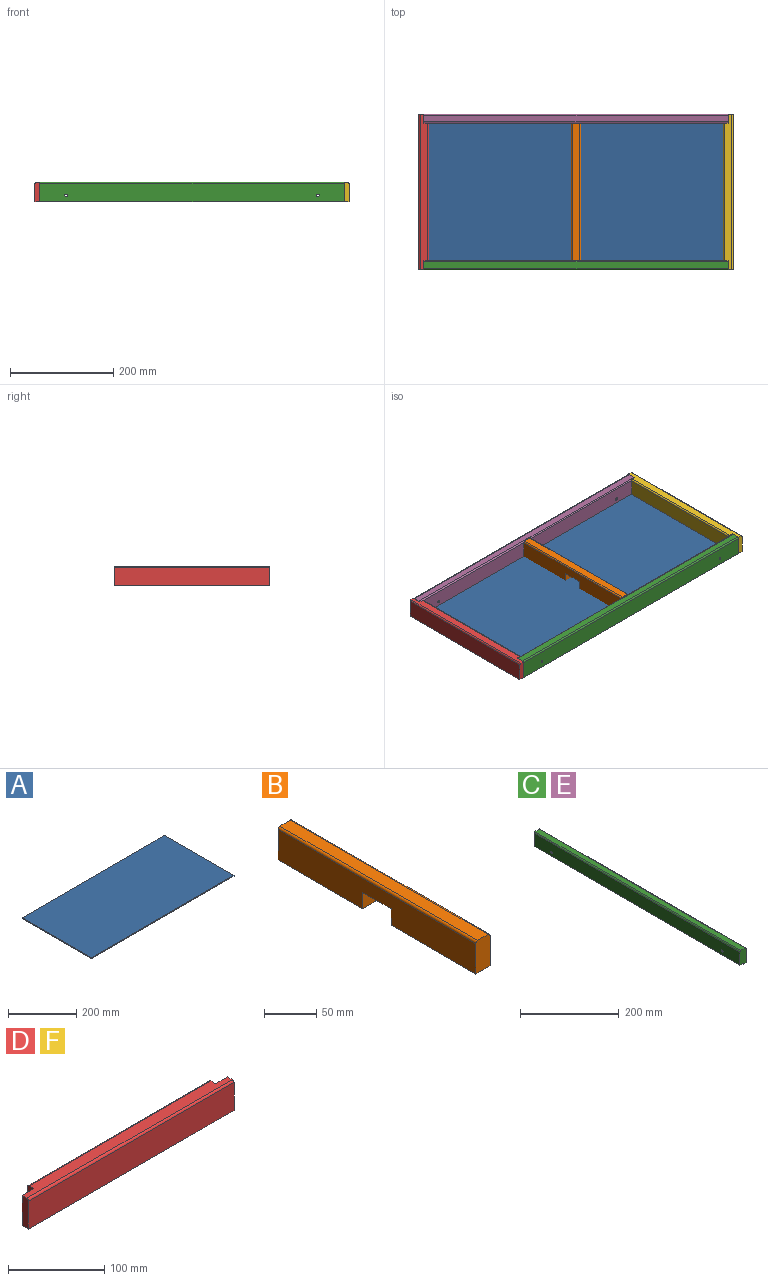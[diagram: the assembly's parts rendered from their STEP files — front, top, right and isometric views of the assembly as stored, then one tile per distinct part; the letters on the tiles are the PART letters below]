
ASSEMBLY  parts=6 mates=5
PART A: 6 faces, bbox 590.6x285.8x3.2 mm
  f0: plane 590.55x3.18mm, normal (0,-1,0), area 1875mm2, adj f1,f3,f4,f5
  f1: plane 285.75x3.18mm, normal (1,0,0), area 907.3mm2, adj f0,f2,f4,f5
  f2: plane 590.55x3.18mm, normal (0,1,0), area 1875mm2, adj f1,f3,f4,f5
  f3: plane 285.75x3.18mm, normal (-1,0,0), area 907.3mm2, adj f0,f2,f4,f5
  f4: plane 590.55x285.75mm, normal (0,0,1), area 168749.7mm2, adj f0,f1,f2,f3
  f5: plane 590.55x285.75mm, normal (0,0,-1), area 168749.7mm2, adj f0,f1,f2,f3
PART B: 12 faces, bbox 19.1x266.7x38.1 mm
  f0: plane 114.3x19.05mm, normal (0,0,-1), area 2177.4mm2, adj f1,f2,f3,f9
  f1: plane 266.7x35.56mm, normal (1,0,0), area 8758mm2, adj f0,f3,f4,f6,f7,f9,f10,f11
  f2: plane 266.7x35.56mm, normal (-1,0,0), area 8758mm2, adj f0,f3,f4,f6,f8,f9,f10,f11
  f3: plane 38.1x19.05mm, normal (0,-1,0), area 723mm2, adj f0,f1,f2,f5,f7,f8
  f4: plane 38.1x19.05mm, normal (0,1,0), area 723mm2, adj f1,f2,f5,f6,f7,f8
  f5: plane 266.7x13.97mm, normal (0,0,1), area 3725.8mm2, adj f3,f4,f7,f8
  f6: plane 114.3x19.05mm, normal (0,0,-1), area 2177.4mm2, adj f1,f2,f4,f10
  f7: cylinder r=2.54mm len=266.7mm, axis (0,-1,0), area 1064.1mm2, adj f1,f3,f4,f5
  f8: cylinder r=2.54mm len=266.7mm, axis (0,1,0), area 1064.1mm2, adj f2,f3,f4,f5
  f9: plane 19.05x19.05mm, normal (0,1,0), area 362.9mm2, adj f0,f1,f2,f11
  f10: plane 19.05x19.05mm, normal (0,-1,0), area 362.9mm2, adj f1,f2,f6,f11
  f11: plane 38.1x19.05mm, normal (0,0,-1), area 725.8mm2, adj f1,f2,f9,f10
PART C: 12 faces, bbox 17.5x590.6x38.1 mm
  f0: plane 590.55x32.39mm, normal (-1,0,0), area 19089.3mm2, adj f1,f7,f8,f9,f10,f11
  f1: plane 590.55x9.53mm, normal (0,0,-1), area 5625mm2, adj f0,f2,f8,f9
  f2: plane 590.55x3.18mm, normal (-1,0,0), area 1875mm2, adj f1,f3,f8,f9
  f3: plane 590.55x7.94mm, normal (0,0,-1), area 4687.5mm2, adj f2,f4,f8,f9
  f4: plane 590.55x35.56mm, normal (1,0,0), area 20964.3mm2, adj f3,f5,f8,f9,f10,f11
  f5: cylinder r=2.54mm len=590.55mm, axis (0,1,0), area 2356.2mm2, adj f4,f6,f8,f9
  f6: plane 590.55x12.38mm, normal (0,0,1), area 7312.5mm2, adj f5,f7,f8,f9
  f7: cylinder r=2.54mm len=590.55mm, axis (0,1,0), area 2356.2mm2, adj f0,f6,f8,f9
  f8: plane 38.1x17.46mm, normal (0,-1,0), area 632.3mm2, adj f0,f1,f2,f3,f4,f5,f6,f7
  f9: plane 38.1x17.46mm, normal (0,1,0), area 632.3mm2, adj f0,f1,f2,f3,f4,f5,f6,f7
  f10: cylinder r=2.38mm len=17.46mm, axis (1,0,0), area 261.3mm2, adj f0,f4
  f11: cylinder r=2.38mm len=17.46mm, axis (1,0,0), area 261.3mm2, adj f0,f4
PART D: 12 faces, bbox 301.8x19.1x38.1 mm
  f0: plane 34.93x9.53mm, normal (-1,0,0), area 331.3mm2, adj f4,f6,f7,f10,f11
  f1: plane 38.1x9.53mm, normal (-1,0,0), area 361.5mm2, adj f2,f4,f7,f8,f9
  f2: plane 301.75x35.56mm, normal (0,-1,0), area 10730.3mm2, adj f1,f3,f8,f9
  f3: plane 38.1x9.53mm, normal (1,0,0), area 361.5mm2, adj f2,f4,f7,f8,f9
  f4: plane 301.75x38.1mm, normal (0,1,0), area 2182.3mm2, adj f0,f1,f3,f5,f7,f8,f11
  f5: plane 34.93x9.53mm, normal (1,0,0), area 331.3mm2, adj f4,f6,f7,f10,f11
  f6: plane 266.7x32.39mm, normal (0,1,0), area 8637.1mm2, adj f0,f5,f10,f11
  f7: plane 301.75x13.97mm, normal (0,0,1), area 3970.6mm2, adj f0,f1,f3,f4,f5,f9,f10
  f8: plane 301.75x9.53mm, normal (0,0,-1), area 2874.2mm2, adj f1,f2,f3,f4
  f9: cylinder r=2.54mm len=301.75mm, axis (-1,0,0), area 1203.9mm2, adj f1,f2,f3,f7
  f10: cylinder r=2.54mm len=266.7mm, axis (1,0,0), area 1064.1mm2, adj f0,f5,f6,f7
  f11: plane 266.7x9.53mm, normal (0,0,-1), area 2540.3mm2, adj f0,f4,f5,f6
PART E: same geometry as C
PART F: same geometry as D
PLACE A t=(-25.02,80.93,9.9)mm fixed
PLACE B t=(-25.02,80.93,10.3)mm
PLACE C rot(axis=(0,0,-1),90deg) t=(270.25,-61.95,30.22)mm
PLACE D rot(axis=(0,0,-1),90deg) t=(-320.3,214.28,9.9)mm
PLACE E rot(axis=(0,0,1),90deg) t=(-320.3,223.8,30.22)mm
PLACE F rot(axis=(0,0,1),90deg) t=(270.25,-52.42,9.9)mm
MATE fastened F.f4 <-> A.f1  axis (-1,0,0) through (270.25,80.93,9.9)mm
MATE fastened B.f4 <-> E.f0  axis (0,1,0) through (-25.02,214.28,29.28)mm
MATE fastened A.f0 <-> C.f2  axis (0,-1,0) through (-25.02,-61.95,11.49)mm
MATE fastened E.f1 <-> A.f4  axis (0,0,-1) through (-25.02,223.8,13.07)mm
MATE fastened D.f11 <-> A.f4  axis (0,0,-1) through (-320.3,80.93,13.07)mm
